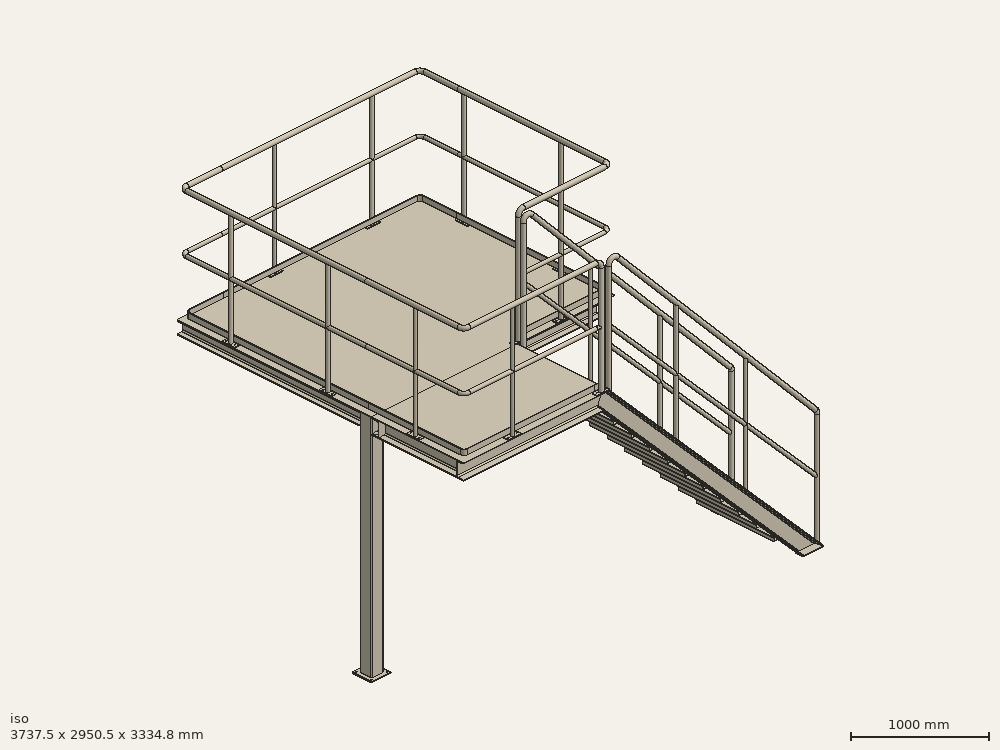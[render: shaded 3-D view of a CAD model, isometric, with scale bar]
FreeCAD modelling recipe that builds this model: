
FCSTD DOCUMENT  (FreeCAD 0.21R33668 +26 (Git))
Label: trestle01a
License: All rights reserved
LicenseURL: http://en.wikipedia.org/wiki/All_rights_reserved
objects: Part::FeaturePython×12, Part::Extrusion×2, Part::MultiFuse×1, Spreadsheet::Sheet×1, Sketcher::SketchObject×1, App::Part×1
note: 13 computed .brp shape members not serialized (recipe doc carries the construction recipe); baked Part::Feature solids carry a one-line shape summary decoded from their .brp

FEATURE [Part::FeaturePython] BasePlate  # WARN: FeaturePython — macro-defined, semantics opaque (R4)
  B = 200
  D = 15
  H = 200
  b1 = 20
  h1 = 20
  sface = 0
FEATURE [Part::Extrusion] Extrude
  Base = -> BasePlate
  Dir = (0,0,1)
  DirMode = 2
  FaceMakerClass = Part::FaceMakerBullseye
  LengthFwd = 10
  LengthRev = 0
  Solid = true
  Symmetric = false
FEATURE [Part::FeaturePython] Square_Pipe  # WARN: FeaturePython — macro-defined, semantics opaque (R4)
  A = 125
  H = 125
  L = 2200
  Solid = true
  g0 = 7.85
  mass = 47.7221
  size = 40
  standard = SS
  expr: L = Spreadsheet.H0
FEATURE [Part::MultiFuse] Fusion  label="PostSq"
  Shapes = -> [Extrude,Square_Pipe]
FEATURE [Part::FeaturePython] Array  label="post"  # Draft array (typed FeaturePython)
  AlwaysSyncPlacement = false
  Angle = 360
  ArrayType = 0
  Axis = (0,0,1)
  Base = -> Fusion
  Center = (0,0,0)
  Count = 4
  ExpandArray = false
  Fuse = false
  IntervalAxis = (0,0,0)
  IntervalX = (2375,0,0)
  IntervalY = (0,1875,0)
  IntervalZ = (0,0,2200)
  NumberCircles = 3
  NumberPolar = 5
  NumberX = 2
  NumberY = 2
  NumberZ = 1
  PlacementList = 4 placements: [(0,0,0),(0,1875,0),(2375,0,0),(2375,1875,0)]
  RadialDistance = 50
  ScaleList = (4) [(1,1,1),(1,1,1),(1,1,1),(1,1,1)]
  Symmetry = 1
  TangentialDistance = 25
  expr: .IntervalX.x = Spreadsheet.W0 - 125
  expr: .IntervalY.y = Spreadsheet.L0 - 125
FEATURE [Part::FeaturePython] HShapeSteel  # WARN: FeaturePython — macro-defined, semantics opaque (R4)
  B = 125
  H = 125
  L = 1875
  Placement = pos=(0,62.5,2137.5) rot=(-1,0,0;1.5708rad)
  Solid = true
  g0 = 7.85
  mass = 44.6175
  size = 1
  standard = SS_Wide
  t1 = 6.5
  t2 = 9
  expr: .Placement.Base.z = Spreadsheet.H0 - 62.5
  expr: L = Spreadsheet.L0 - 125
FEATURE [Part::FeaturePython] Array001  label="beam_v"  # Draft array (typed FeaturePython)
  AlwaysSyncPlacement = false
  Angle = 360
  ArrayType = 0
  Axis = (0,0,1)
  Base = -> HShapeSteel
  Center = (0,0,0)
  Count = 2
  ExpandArray = false
  Fuse = false
  IntervalAxis = (0,0,0)
  IntervalX = (2375,0,0)
  IntervalY = (0,100,0)
  IntervalZ = (0,0,100)
  NumberCircles = 3
  NumberPolar = 5
  NumberX = 2
  NumberY = 1
  NumberZ = 1
  PlacementList = 2 placements: [(0,62.5,2137.5),(2375,62.5,2137.5)]
  RadialDistance = 50
  ScaleList = (2) [(1,1,1),(1,1,1)]
  Symmetry = 1
  TangentialDistance = 25
  expr: .IntervalX.x = Spreadsheet.W0 - 125
FEATURE [Part::FeaturePython] HShapeSteel001  # WARN: FeaturePython — macro-defined, semantics opaque (R4)
  B = 125
  H = 125
  L = 2250
  Placement = pos=(62.5,0,2137.5) rot=(0.57735,-0.57735,0.57735;4.18879rad)
  Solid = true
  g0 = 7.85
  mass = 53.5411
  size = 1
  standard = SS_Wide
  t1 = 6.5
  t2 = 9
  expr: .Placement.Base.z = Spreadsheet.H0 - 62.5
  expr: L = Spreadsheet.W0 - 125 * 2
FEATURE [Part::FeaturePython] Array002  label="beam_h"  # Draft array (typed FeaturePython)
  AlwaysSyncPlacement = false
  Angle = 360
  ArrayType = 0
  Axis = (0,0,1)
  Base = -> HShapeSteel001
  Center = (0,0,0)
  Count = 2
  ExpandArray = false
  Fuse = false
  IntervalAxis = (0,0,0)
  IntervalX = (100,0,0)
  IntervalY = (0,1875,0)
  IntervalZ = (0,0,100)
  NumberCircles = 3
  NumberPolar = 5
  NumberX = 1
  NumberY = 2
  NumberZ = 1
  PlacementList = 2 placements: [(62.5,0,2137.5),(62.5,1875,2137.5)]
  RadialDistance = 50
  ScaleList = (2) [(1,1,1),(1,1,1)]
  Symmetry = 1
  TangentialDistance = 25
  expr: .IntervalY.y = Spreadsheet.L0 - 125
FEATURE [Spreadsheet::Sheet] Spreadsheet
  cells = A2='W; B2(W0)=2500; A3='L; B3(L0)=2000; A4='H; B4(H0)=2200
FEATURE [Sketcher::SketchObject] Sketch
  FullyConstrained = true
  expr: Constraints[8] = Spreadsheet.L0
  expr: Constraints[9] = Spreadsheet.W0
  sketch-geometry (4):
    g0: LineSegment StartX=-62.5 StartY=-62.5 StartZ=0 EndX=2437.5 EndY=-62.5 EndZ=0
    g1: LineSegment StartX=2437.5 StartY=-62.5 StartZ=0 EndX=2437.5 EndY=1937.5 EndZ=0
    g2: LineSegment StartX=2437.5 StartY=1937.5 StartZ=0 EndX=-62.5 EndY=1937.5 EndZ=0
    g3: LineSegment StartX=-62.5 StartY=1937.5 StartZ=0 EndX=-62.5 EndY=-62.5 EndZ=0
  constraints (12):
    c: Coincident(g0,g1)
    c: Coincident(g1,g2)
    c: Coincident(g2,g3)
    c: Coincident(g3,g0)
    c: Horizontal(g0)
    c: Horizontal(g2)
    c: Vertical(g1)
    c: Vertical(g3)
    c: DistanceY(g3,g3) = 2000
    c: DistanceX(g2,g2) = 2500
    c: DistanceY(g0,g-1) = 62.5
    c: DistanceX(g0,g-1) = 62.5
FEATURE [Part::Extrusion] Extrude001  label="chpl"
  Base = -> Sketch
  Dir = (0,0,1)
  DirMode = 2
  FaceMakerClass = Part::FaceMakerBullseye
  LengthFwd = 4.5
  LengthRev = 0
  Placement = pos=(0,0,2200) rot=(0,0,1;0rad)
  Solid = true
  Symmetric = false
  expr: .Placement.Base.z = Spreadsheet.H0
FEATURE [Part::FeaturePython] stair  # WARN: FeaturePython — macro-defined, semantics opaque (R4)
  ClockWise = true
  H = 2200
  L = 2200
  L1 = 1500
  MdlFloor = false
  Placement = pos=(3637.5,-937.5,0) rot=(0,0,1;3.14159rad)
  Rail = 0
  body = 299.842
  handrail = 57.5144
  mass = 357.356
  size = 1
  story = 2
  t = 9
  t0 = 0
  type = 1
  w0 = 800
  w1 = 950
  w2 = 0
  w3 = 0
  expr: .Placement.Base.x = Spreadsheet.H0 + 1500 - 62.5
  expr: H = Spreadsheet.H0
  expr: L = Spreadsheet.H0
FEATURE [Part::FeaturePython] Corner_with_end  # WARN: FeaturePython — macro-defined, semantics opaque (R4)
  Placement = pos=(1373,-987,2204.5) rot=(0,0,1;3.14159rad)
  Reverse = true
  g0 = 7.85
  h = 1100
  k = -90
  l1 = 1410
  l2 = 1000
  mass = 29.375
  p = 1000
  spec = 0
  type = 1
  expr: .Placement.Base.z = Spreadsheet.H0 + 4.5
FEATURE [Part::FeaturePython] Corner  # WARN: FeaturePython — macro-defined, semantics opaque (R4)
  Placement = pos=(-37,13,2204.5) rot=(0,0,1;1.5708rad)
  Reverse = true
  g0 = 7.85
  h = 1100
  k = -90
  l1 = 1900
  l2 = 400
  mass = 24.3651
  p = 1000
  spec = 0
  type = 2
  expr: .Placement.Base.z = Spreadsheet.H0 + 4.5
  expr: l1 = Spreadsheet.L0 - 100
FEATURE [Part::FeaturePython] Corner001  # WARN: FeaturePython — macro-defined, semantics opaque (R4)
  Placement = pos=(363,1913,2204.5) rot=(0,0,1;0rad)
  Reverse = true
  g0 = 7.85
  h = 1100
  k = -90
  l1 = 2050
  l2 = 400
  mass = 25.5905
  p = 1000
  spec = 0
  type = 2
  expr: .Placement.Base.y = Spreadsheet.L0 - 87
  expr: .Placement.Base.z = Spreadsheet.H0 + 4.5
  expr: l1 = Spreadsheet.W0 - 450
FEATURE [Part::FeaturePython] Corner_with_end001  # WARN: FeaturePython — macro-defined, semantics opaque (R4)
  Placement = pos=(1473,-37,2204.5) rot=(0,0,1;0rad)
  Reverse = false
  g0 = 7.85
  h = 1100
  k = 90
  l1 = 940
  l2 = 1550
  mass = 32.9422
  p = 1000
  spec = 0
  type = 1
  expr: .Placement.Base.z = Spreadsheet.H0 + 4.5
  expr: l1 = Spreadsheet.W0 - 1560
  expr: l2 = Spreadsheet.L0 - 450
FEATURE [App::Part] Part  label="Trstle"
  Group = -> [HShapeSteel001,Array002,HShapeSteel,Array001,Fusion,Square_Pipe,BasePlate,Extrude,Array,Spreadsheet,Sketch,Extrude001,stair,Corner_with_end,Corner,Corner001,Corner_with_end001]
  Origin = -> Origin
